# Revit family: rba-bim-B35883
name_source: partatom
category: Plumbing Fixtures
revit_build: Autodesk Revit 2018 (Build: 20170223_1515(x64)
units: mm (PartAtom-declared; Revit-internal decimal feet)

## family parameters
Cut with Voids When Loaded = No
Host = Face
OmniClass Number = 23.40.20.21.21
OmniClass Title = Toilet Paper Dispensers
Part Type = Normal
Room Calculation Point = No
Round Connector Dimension = Use Diameter
Shared = Yes

## types (1)
- B-35883
    ADA Compliant = Yes
    Assembly Code = E1090900
    Default Elevation = 635 mm
    Description = TrimLineSeries™ Recessed Multi-Roll Toilet Tissue Dispenser
    Height = 214.31 mm
    Installation Type = Recessed
    Length = 114.3 mm
    Manufacturer = Bobrick Washroom Equipment, Inc.
    Materials and Finishes = Stainless Steel Type 304 Satin Finish
    Model = B35883
    Modified Issue = 20200916.01
    Price = Prices may vary. Please consult Manufacturer Representative for most up-to-date price list.
    Product Documentation Link = http://bobrick.com
    Product Page URL = http://bobrick.com
    Specification = Recessed multi-roll toilet tissue dispenser shall be Type-304 stainless steel with all-welded construction; exposed surfaces shall have satin fi nish. Door shall be Type-304, 20-gauge (0.9mm) secured to cabinet with two rivets; and equipped with a tumbler lock keyed like other Bobrick washroom accessories. Spindle shall be Type-304, 18-gauge (1.2mm), 1" diameter (25mm) stainless steel. Theft resistant, removable with key provided.
    URL = www.rba.com.au
    Warranty Information = 1 Year Limited Warranty
    Width = 346.08 mm

## geometry (parser evidence)
native form markers: Sweep x3
no freeform markers — native parametric forms only
